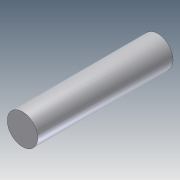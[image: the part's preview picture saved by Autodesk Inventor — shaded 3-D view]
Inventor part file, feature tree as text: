
AUTODESK INVENTOR PART (.ipt)
format: ipt  version: unknown  size: 157,696 bytes
history: native  units: in
note: dims shown in document units (in); Inventor stores cm internally (conversion verified against a paired STEP export)
features: extrude x1, sketch x1
ambient origin geometry x8: Origin, YZ Plane, XZ Plane, XY Plane, X Axis, Y Axis, Z Axis, Center Point
feature tree (2):
  extrude  "Extrusion2"  Depth=5.0in TaperAngle=0.0deg
  sketch  "Sketch2"  dims[d3=1.125in d4=5.0in d5=0.0in]
